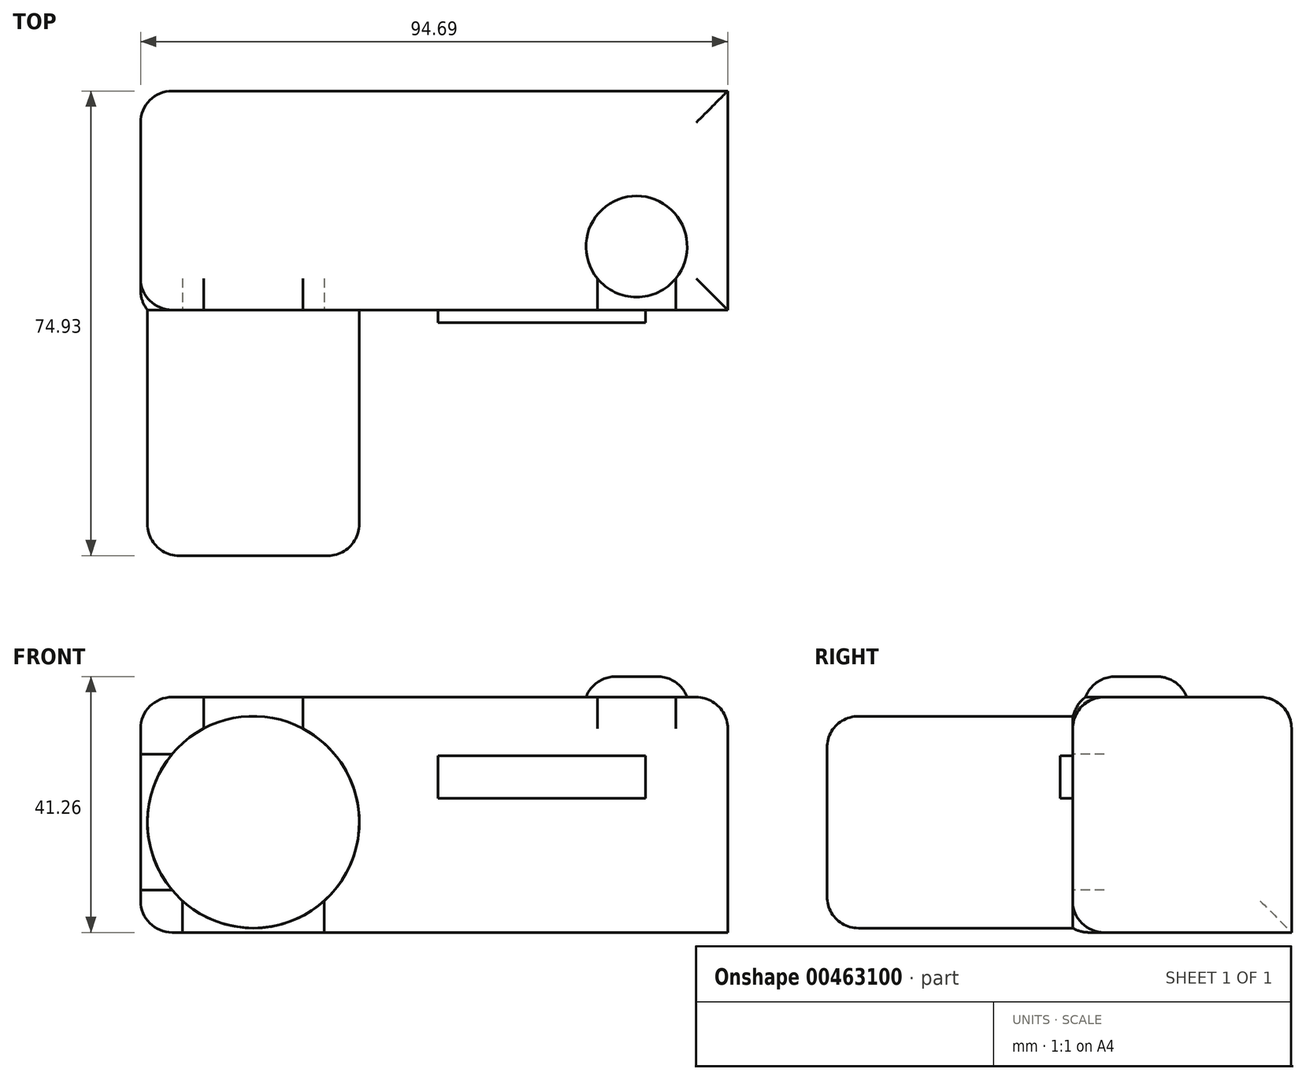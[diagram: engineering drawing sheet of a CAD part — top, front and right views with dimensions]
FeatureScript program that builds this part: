
annotation { "Feature Type Name" : "Feature", "Feature Type Description" : "" }
export const myFeature = defineFeature(function(context is Context, id is Id, definition is map)
    precondition{}
    {
        {
            var Q0;
            Q0=qCreatedBy(makeId("Front.planeOp"),FACE);
            var sketch = newSketch(context, id + "F0", { "sketchPlane" : qUnion([Q0])});
            skLineSegment(sketch, "E0.bottom", {"start": v(-79.99, 21.88) * mm, "end": v(14.7, 21.88) * mm});
            skLineSegment(sketch, "E0.top", {"start": v(-79.99, -16.08) * mm, "end": v(14.7, -16.08) * mm});
            skLineSegment(sketch, "E0.left", {"start": v(-79.99, 21.88) * mm, "end": v(-79.99, -16.08) * mm});
            skLineSegment(sketch, "E0.right", {"start": v(14.7, 21.88) * mm, "end": v(14.7, -16.08) * mm});
            skSolve(sketch);
        }
        {
            var Q0;
            Q0=makeQuery(id+"F0.imprint","IMPRINT",FACE,{"disambiguationData":[TD([[makeQuery(id+"F0.imprint","IMPRINT",EDGE,{"derivedFrom":sQuery(id+"F0.wireOp",EDGE,"E0.bottom")}),-1.0]])]});
            extrude(context, id + "F1", {"entities" : qUnion([Q0]), "depth" : 35.3 * mm});
        }
        {
            var Q0;
            Q0=makeQuery(id+"F1.opExtrude","CAP_FACE",FACE,{"disambiguationData":[OSD([sQuery(id+"F0.wireOp",EDGE,"E0.bottom"),sQuery(id+"F0.wireOp",EDGE,"E0.top"),sQuery(id+"F0.wireOp",EDGE,"E0.left"),sQuery(id+"F0.wireOp",EDGE,"E0.right")])],"isStart":false});
            var sketch = newSketch(context, id + "F2", { "sketchPlane" : qUnion([Q0])});
            skCircle(sketch, "E1", {"center": v(-61.8, 1.7) * mm, "radius": 17.08 * mm});
            skSolve(sketch);
        }
        {
            var Q0;
            Q0=makeQuery(id+"F2.imprint","IMPRINT",FACE,{"disambiguationData":[TD([[makeQuery(id+"F2.imprint","IMPRINT",EDGE,{"derivedFrom":sQuery(id+"F2.wireOp",EDGE,"E1")}),1.0]])]});
            extrude(context, id + "F3", {"entities" : qUnion([Q0]), "operationType" : NewBodyOperationType.ADD, "depth" : 39.62 * mm});
        }
        {
            var Q0;
            Q0=makeQuery(id+"F1.opExtrude","SWEPT_FACE",FACE,{"disambiguationData":[OSD([sQuery(id+"F0.wireOp",EDGE,"E0.bottom")])]});
            var sketch = newSketch(context, id + "F4", { "sketchPlane" : qUnion([Q0])});
            skCircle(sketch, "E2", {"center": v(0, -25.08) * mm, "radius": 8.15 * mm});
            skSolve(sketch);
        }
        {
            var Q0;
            Q0=makeQuery(id+"F4.imprint","IMPRINT",FACE,{"disambiguationData":[TD([[makeQuery(id+"F4.imprint","IMPRINT",EDGE,{"derivedFrom":sQuery(id+"F4.wireOp",EDGE,"E2")}),1.0]])]});
            extrude(context, id + "F5", {"entities" : qUnion([Q0]), "operationType" : NewBodyOperationType.ADD, "depth" : 3.3 * mm});
        }
        {
            var Q0;
            Q0=makeQuery(id+"F1.opExtrude","CAP_EDGE",EDGE,{"disambiguationData":[OSD([sQuery(id+"F0.wireOp",EDGE,"E0.bottom")])],"isStart":false});
            var Q1;
            Q1=makeQuery(id+"F1.opExtrude","SWEPT_EDGE",EDGE,{"disambiguationData":[OSD([sQuery(id+"F0.wireOp",EDGE,"E0.bottom"),sQuery(id+"F0.wireOp",EDGE,"E0.left")])]});
            var Q2;
            Q2=makeQuery(id+"F1.opExtrude","CAP_EDGE",EDGE,{"disambiguationData":[OSD([sQuery(id+"F0.wireOp",EDGE,"E0.bottom")])],"isStart":true});
            var Q3;
            Q3=makeQuery(id+"F1.opExtrude","SWEPT_EDGE",EDGE,{"disambiguationData":[OSD([sQuery(id+"F0.wireOp",EDGE,"E0.bottom"),sQuery(id+"F0.wireOp",EDGE,"E0.right")])]});
            var Q4;
            Q4=makeQuery(id+"F5.opExtrude","CAP_EDGE",EDGE,{"disambiguationData":[OSD([sQuery(id+"F4.wireOp",EDGE,"E2")])],"isStart":false});
            var Q5;
            Q5=makeQuery(id+"F3.opExtrude","CAP_EDGE",EDGE,{"disambiguationData":[OSD([sQuery(id+"F2.wireOp",EDGE,"E1")])],"isStart":false});
            fillet(context, id + "F6", {"entities" : qUnion([Q0, Q1, Q2, Q3, Q4, Q5]), "radius" : 5.08 * mm, "tangentPropagation" : true, "allowEdgeOverflow" : false});
        }
        {
            var Q0;
            Q0=makeQuery(id+"F1.opExtrude","CAP_FACE",FACE,{"disambiguationData":[OSD([sQuery(id+"F0.wireOp",EDGE,"E0.bottom"),sQuery(id+"F0.wireOp",EDGE,"E0.top"),sQuery(id+"F0.wireOp",EDGE,"E0.left"),sQuery(id+"F0.wireOp",EDGE,"E0.right")])],"isStart":false});
            var sketch = newSketch(context, id + "F7", { "sketchPlane" : qUnion([Q0])});
            skLineSegment(sketch, "E3.bottom", {"start": v(-32.04, 12.4) * mm, "end": v(1.43, 12.4) * mm});
            skLineSegment(sketch, "E3.top", {"start": v(-32.04, 5.57) * mm, "end": v(1.43, 5.57) * mm});
            skLineSegment(sketch, "E3.left", {"start": v(-32.04, 12.4) * mm, "end": v(-32.04, 5.57) * mm});
            skLineSegment(sketch, "E3.right", {"start": v(1.43, 12.4) * mm, "end": v(1.43, 5.57) * mm});
            skSolve(sketch);
        }
        {
            var Q0;
            Q0=makeQuery(id+"F7.imprint","IMPRINT",FACE,{"disambiguationData":[TD([[makeQuery(id+"F7.imprint","IMPRINT",EDGE,{"derivedFrom":sQuery(id+"F7.wireOp",EDGE,"E3.bottom")}),-1.0]])]});
            extrude(context, id + "F8", {"entities" : qUnion([Q0]), "operationType" : NewBodyOperationType.ADD, "depth" : 2.03 * mm});
        }
        {
            var Q0;
            Q0=makeQuery(id+"F1.opExtrude","CAP_EDGE",EDGE,{"disambiguationData":[OSD([sQuery(id+"F0.wireOp",EDGE,"E0.left")])],"isStart":false});
            fillet(context, id + "F9", {"entities" : qUnion([Q0]), "radius" : 5.08 * mm, "tangentPropagation" : true, "allowEdgeOverflow" : false});
        }
        {
            var Q0;
            Q0=makeQuery(id+"F1.opExtrude","SWEPT_FACE",FACE,{"disambiguationData":[OSD([sQuery(id+"F0.wireOp",EDGE,"E0.left")])]});
            var Q1;
            Q1=makeQuery(id+"F1.opExtrude","CAP_EDGE",EDGE,{"disambiguationData":[OSD([sQuery(id+"F0.wireOp",EDGE,"E0.left")])],"isStart":true});
            fillet(context, id + "F10", {"entities" : qUnion([Q0, Q1]), "radius" : 5.08 * mm, "tangentPropagation" : true, "allowEdgeOverflow" : false});
        }
    });
